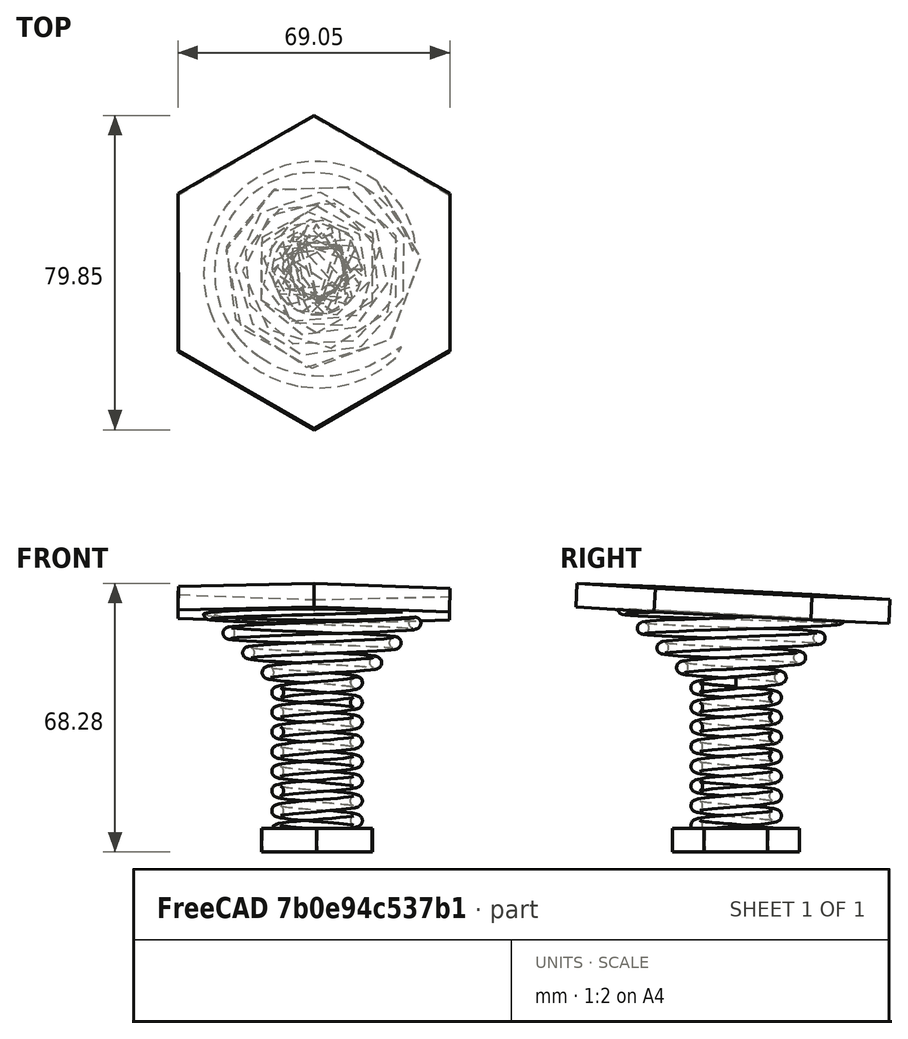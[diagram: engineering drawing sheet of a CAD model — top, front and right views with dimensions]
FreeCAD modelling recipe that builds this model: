
FCSTD DOCUMENT  (FreeCAD 0.21R33668 +26 (Git))
Label: Ressort-essai2-1-FEM-2-1
License: All rights reserved
LicenseURL: http://en.wikipedia.org/wiki/All_rights_reserved
objects: Sketcher::SketchObject×3, Part::Helix×2, Part::Sweep×2, PartDesign::Plane×2, PartDesign::Pad×2, PartDesign::Body×2, PartDesign::ShapeBinder×1, Part::MultiFuse×1, App::MaterialObjectPython×1, Fem::FemMeshShapeNetgenObject×1, Fem::ConstraintFixed×1, Fem::ConstraintForce×1, Fem::FemSolverObjectPython×1, Fem::FemResultObjectPython×1, Fem::FemAnalysis×1
note: 17 computed .brp shape members not serialized (recipe doc carries the construction recipe); baked Part::Feature solids carry a one-line shape summary decoded from their .brp

FEATURE [Part::Helix] Helix  label="Hélice"
  Angle = 0
  AttacherType = Attacher::AttachEngine3D
  Height = 40
  LocalCoord = 0
  Pitch = 5
  Radius = 10
  SegmentLength = 0
  Style = 1
FEATURE [Sketcher::SketchObject] Sketch  label="Profile"
  FullyConstrained = true
  MapMode = 5
  Placement = pos=(0,0,0) rot=(1,0,0;1.5708rad)
  Support = -> [XZ_Plane]
  sketch-geometry (1):
    g0: Circle CenterX=10 CenterY=0 CenterZ=0 NormalX=0 NormalY=0 NormalZ=1 AngleXU=0 Radius=1.5
  constraints (3):
    c: PointOnObject(g0,g-1)
    c: Radius(g0) = 1.5
    c: DistanceX(g-1,g0) = 10
FEATURE [Part::Sweep] Sweep
  Frenet = true
  Sections = -> [Sketch]
  Solid = true
  Spine = -> Helix
  Transition = 1
FEATURE [Part::Helix] Helix001  label="Hélice001"
  Angle = 45
  AttacherType = Attacher::AttachEngine3D
  Height = 20
  LocalCoord = 0
  Pitch = 5
  Placement = pos=(0,0,40) rot=(0,0,1;0rad)
  Radius = 10
  SegmentLength = 0
  Style = 1
FEATURE [Part::Sweep] Sweep001
  Frenet = true
  Placement = pos=(0,0,40) rot=(0,0,1;0rad)
  Sections = -> [Sketch]
  Solid = true
  Spine = -> Helix001
  Transition = 1
FEATURE [PartDesign::Plane] DatumPlane
  Length = 60
  MapMode = 3
  Placement = pos=(0,0,0) rot=(1,0,0;3.14159rad)
  ResizeMode = 0
  Support = -> [Sketch]
  Width = 60
FEATURE [Sketcher::SketchObject] Sketch001
  FullyConstrained = false
  MapMode = 5
  Placement = pos=(0,0,0) rot=(1,0,0;3.14159rad)
  Support = -> [DatumPlane]
  sketch-geometry (7):
    g0: LineSegment StartX=13.9076 StartY=8.18793 StartZ=0 EndX=-0.137134 EndY=16.1383 EndZ=0
    g1: LineSegment StartX=-0.137134 StartY=16.1383 StartZ=0 EndX=-14.0448 EndY=7.95041 EndZ=0
    g2: LineSegment StartX=-14.0448 StartY=7.95041 StartZ=0 EndX=-13.9076 EndY=-8.18793 EndZ=0
    g3: LineSegment StartX=-13.9076 StartY=-8.18793 StartZ=0 EndX=0.137134 EndY=-16.1383 EndZ=0
    g4: LineSegment StartX=0.137134 StartY=-16.1383 StartZ=0 EndX=14.0448 EndY=-7.95041 EndZ=0
    g5: LineSegment StartX=14.0448 StartY=-7.95041 StartZ=0 EndX=13.9076 EndY=8.18793 EndZ=0
    g6: Circle CenterX=0 CenterY=0 CenterZ=0 NormalX=0 NormalY=0 NormalZ=1 AngleXU=0 Radius=16.1389
  constraints (14):
    c: Coincident(g0,g1)
    c: Coincident(g1,g2)
    c: Coincident(g2,g3)
    c: Coincident(g3,g4)
    c: Coincident(g4,g5)
    c: Coincident(g5,g0)
    c: Equal(g0, g1-g5) x5
    c: PointOnObject(g0,g6)
    c: PointOnObject(g1,g6)
    c: PointOnObject(g2,g6)
    c: PointOnObject(g3,g6)
    c: PointOnObject(g4,g6)
    c: PointOnObject(g5,g6)
    c: Coincident(g6,g-1)
FEATURE [PartDesign::Pad] Pad
  Direction = (0,-2e-16,-1)
  Length = 6
  Length2 = 10
  Midplane = true
  Placement = pos=(0,0,0) rot=(1,0,0;3.14159rad)
  Profile = -> Sketch001
  ReferenceAxis = -> Sketch001 [N_Axis]
  Type = 0
FEATURE [PartDesign::Body] Body
  Group = -> [Sketch,DatumPlane,Sketch001,Pad]
  Origin = -> Origin
  Tip = -> Pad
FEATURE [PartDesign::ShapeBinder] ReferenceSweep001
  Placement = pos=(0,0,40) rot=(0,0,1;0rad)
  Support = -> [Sweep001]
  TraceSupport = false
FEATURE [PartDesign::Plane] DatumPlane001
  Length = 97.5241
  MapMode = 8
  Placement = pos=(31.2223,-2.01915,60.0415) rot=(0.999638,0.026587,-0.004143;3.08931rad)
  ResizeMode = 0
  Support = -> [ReferenceSweep001]
  Width = 109.064
FEATURE [Sketcher::SketchObject] Sketch002
  FullyConstrained = false
  MapMode = 5
  Placement = pos=(31.2223,-2.01915,60.0415) rot=(0.999638,0.026587,-0.004143;3.08931rad)
  Support = -> [DatumPlane001]
  sketch-geometry (7):
    g0: LineSegment StartX=3.5913 StartY=-20.9796 StartZ=0 EndX=1.49521 EndY=18.7911 EndZ=0
    g1: LineSegment StartX=1.49521 StartY=18.7911 StartZ=0 EndX=-33.9952 EndY=36.8611 EndZ=0
    g2: LineSegment StartX=-33.9952 StartY=36.8611 StartZ=0 EndX=-67.3896 EndY=15.1605 EndZ=0
    g3: LineSegment StartX=-67.3896 StartY=15.1605 StartZ=0 EndX=-65.2935 EndY=-24.6101 EndZ=0
    g4: LineSegment StartX=-65.2935 StartY=-24.6101 StartZ=0 EndX=-29.803 EndY=-42.6802 EndZ=0
    g5: LineSegment StartX=-29.803 StartY=-42.6802 StartZ=0 EndX=3.5913 EndY=-20.9796 EndZ=0
    g6: Circle CenterX=-31.8991 CenterY=-2.90951 CenterZ=0 NormalX=0 NormalY=0 NormalZ=1 AngleXU=0 Radius=39.8259
  constraints (13):
    c: Coincident(g0,g1)
    c: Coincident(g1,g2)
    c: Coincident(g2,g3)
    c: Coincident(g3,g4)
    c: Coincident(g4,g5)
    c: Coincident(g5,g0)
    c: Equal(g0, g1-g5) x5
    c: PointOnObject(g0,g6)
    c: PointOnObject(g1,g6)
    c: PointOnObject(g2,g6)
    c: PointOnObject(g3,g6)
    c: PointOnObject(g4,g6)
    c: PointOnObject(g5,g6)
FEATURE [PartDesign::Pad] Pad001
  Direction = (-0.00688828,-0.0524625,-0.998599)
  Length = 6
  Length2 = 10
  Midplane = true
  Placement = pos=(31.2223,-2.01915,60.0415) rot=(0.999638,0.026587,-0.004143;3.08931rad)
  Profile = -> Sketch002
  ReferenceAxis = -> Sketch002 [N_Axis]
  Type = 0
FEATURE [PartDesign::Body] Body001  label="Corps"
  Group = -> [DatumPlane001,ReferenceSweep001,Sketch002,Pad001]
  Origin = -> Origin001
  Tip = -> Pad001
FEATURE [Part::MultiFuse] Fusion
  Shapes = -> [Body,Sweep,Sweep001,Body001]
FEATURE [App::MaterialObjectPython] MaterialSolid  # material (typed FeaturePython)
  Category = 0
  Material = AuthorAndLicense=(c) 2013 Juergen Riegel (CC-BY 3.0); CardName=CalculiX-Steel; Density=7900 kg/m^3; Description=Standard steel material for CalculiX sample calculations; Father=Metal; Name=CalculiX-Steel; PoissonRatio=0.3; SpecificHeat=590 J/kg/K; ThermalConductivity=43 W/m/K; ThermalExpansionCoefficient=0.000012 m/m/K; YoungsModulus=210000 MPa
FEATURE [Fem::FemMeshShapeNetgenObject] FEMMeshNetgen
  Fineness = 0
  GrowthRate = 0.3
  MaxSize = 1000
  NbSegsPerEdge = 1
  NbSegsPerRadius = 2
  Optimize = false
  SecondOrder = true
  Shape = -> Fusion
FEATURE [Fem::ConstraintFixed] ConstraintFixed
  NormalDirection = (0.00688828,0.0524625,0.998599)
  Normals = (4) [(0.00688828,0.0524625,0.998599),(0.00688828,0.0524625,0.998599),(0.00688828,0.0524625,0.998599),(0.00688828,0.0524625,0.998599)]
  Points = (4) [(10.7359,-13.909,63.8117),(10.7359,12.605,62.4188),(-12.2663,-13.9007,63.9699),(-12.2663,12.6133,62.577)]
  References = -> [Fusion]
  Scale = 8
FEATURE [Fem::ConstraintForce] ConstraintForce
  DirectionVector = (0,-4e-16,-1)
  Force = 9000000
  NormalDirection = (0,-4e-16,-1)
  Points = (4) [(4.68159,-5.37945,-3),(4.68159,5.37945,-3),(-4.68159,-5.37945,-3),(-4.68159,5.37945,-3)]
  References = -> [Fusion]
  Scale = 4
FEATURE [Fem::FemSolverObjectPython] SolverCcxTools  # FEM object (typed FeaturePython)
  AnalysisType = 4
  BeamShellResultOutput3D = false
  BucklingFactors = 1
  EigenmodeHighLimit = 1000000
  EigenmodeLowLimit = 0
  EigenmodesCount = 10
  GeometricalNonlinearity = 0
  IterationsControlParameterCutb = 0.25,0.5,0.75,0.85,,,1.5,
  IterationsControlParameterIter = 4,8,9,200,10,400,,200,,
  IterationsControlParameterTimeUse = false
  IterationsThermoMechMaximum = 200
  IterationsUserDefinedIncrementations = false
  IterationsUserDefinedTimeStepLength = false
  MaterialNonlinearity = 0
  MatrixSolverType = 0
  SplitInputWriter = false
  ThermoMechSteadyState = true
  TimeEnd = 1
  TimeInitialStep = 1
FEATURE [Fem::FemResultObjectPython] CCX__Results  # FEM object (typed FeaturePython)
  Eigenmode = 0
  EigenmodeFrequency = 0
  NodeNumbers = [0]
  ResultType = Fem::ResultMechanical
  Stats = [0,0,0,0,0,0,0,0,0,0,0,0,0,0,0,0,0,0,0,0,0,0,0,0,0,0]
  Time = 0
FEATURE [Fem::FemAnalysis] Analysis
  Group = -> [MaterialSolid,FEMMeshNetgen,ConstraintFixed,ConstraintForce,SolverCcxTools,CCX__Results]
